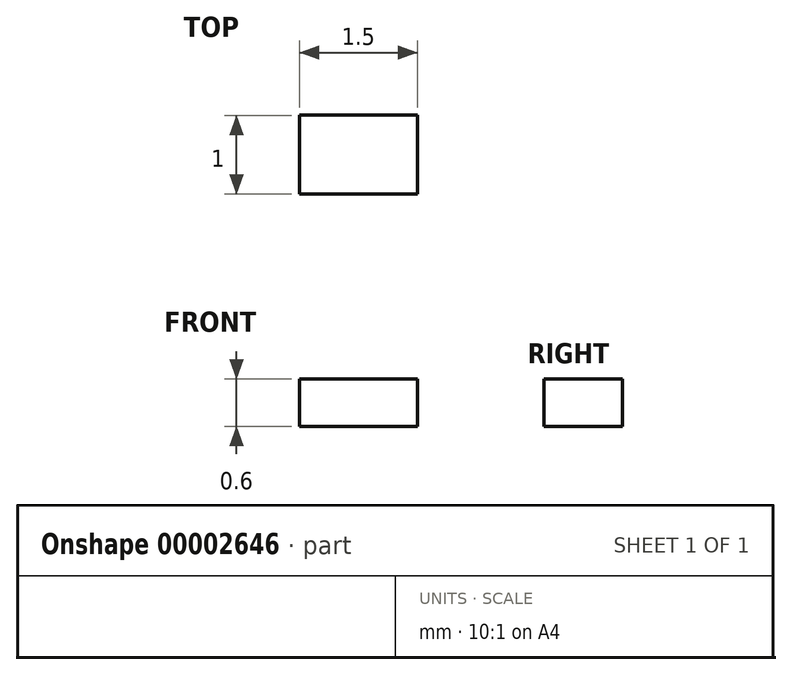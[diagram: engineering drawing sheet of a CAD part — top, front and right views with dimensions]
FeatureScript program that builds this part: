
annotation { "Feature Type Name" : "Feature", "Feature Type Description" : "" }
export const myFeature = defineFeature(function(context is Context, id is Id, definition is map)
    precondition{}
    {
        {
            var Q0;
            Q0=qCreatedBy(makeId("Top.planeOp"),FACE);
            var sketch = newSketch(context, id + "F0", { "sketchPlane" : qUnion([Q0])});
            skLineSegment(sketch, "E0.bottom", {"start": v(-0.75, 1.48) * mm, "end": v(0.75, 1.48) * mm});
            skLineSegment(sketch, "E0.top", {"start": v(-0.75, 0.48) * mm, "end": v(0.75, 0.48) * mm});
            skLineSegment(sketch, "E0.left", {"start": v(-0.75, 1.48) * mm, "end": v(-0.75, 0.48) * mm});
            skLineSegment(sketch, "E0.right", {"start": v(0.75, 1.48) * mm, "end": v(0.75, 0.48) * mm});
            skSolve(sketch);
        }
        {
            var Q0;
            Q0=makeQuery(id+"F0.imprint","IMPRINT",FACE,{"disambiguationData":[TD([[makeQuery(id+"F0.imprint","IMPRINT",EDGE,{"derivedFrom":sQuery(id+"F0.wireOp",EDGE,"E0.bottom")}),-1.0]])]});
            extrude(context, id + "F1", {"entities" : qUnion([Q0]), "depth" : .6 * mm});
        }
    });
